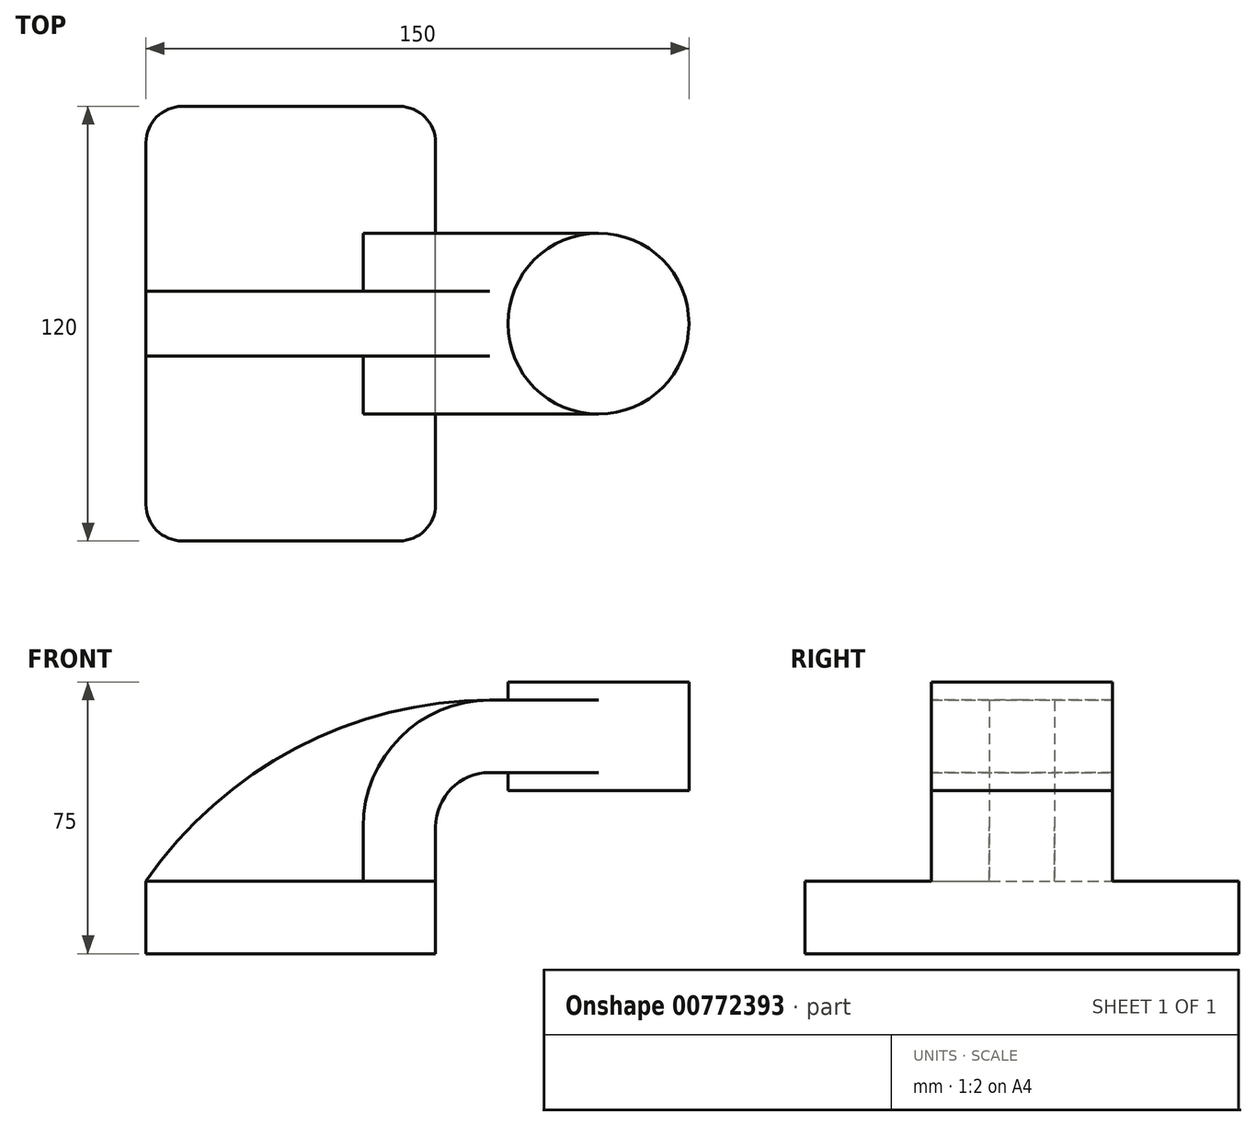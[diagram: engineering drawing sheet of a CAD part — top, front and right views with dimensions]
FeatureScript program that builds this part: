
annotation { "Feature Type Name" : "Feature", "Feature Type Description" : "" }
export const myFeature = defineFeature(function(context is Context, id is Id, definition is map)
    precondition{}
    {
        {
            var Q0;
            Q0=qCreatedBy(makeId("Front.planeOp"),FACE);
            var sketch = newSketch(context, id + "F0", { "sketchPlane" : qUnion([Q0])});
            skLineSegment(sketch, "E0.bottom", {"start": v(0, 0) * mm, "end": v(80, 0) * mm});
            skLineSegment(sketch, "E0.top", {"start": v(0, 20) * mm, "end": v(80, 20) * mm});
            skLineSegment(sketch, "E0.left", {"start": v(0, 0) * mm, "end": v(0, 20) * mm});
            skLineSegment(sketch, "E0.right", {"start": v(80, 0) * mm, "end": v(80, 20) * mm});
            skLineSegment(sketch, "E1", {"start": v(80, 20) * mm, "end": v(80, 35) * mm});
            skLineSegment(sketch, "E2", {"start": v(95, 50) * mm, "end": v(125, 50) * mm});
            skPoint(sketch, "E3.visualSharp", {"position": v(80, 50) * mm});
            skArc(sketch, "E3.filletArc", {"start": v(95, 50) * mm, "mid": v(84.4, 45.6) * mm, "end": v(80, 35) * mm});
            skLineSegment(sketch, "E4.bottom", {"start": v(125, 45) * mm, "end": v(150, 45) * mm});
            skLineSegment(sketch, "E4.top", {"start": v(125, 75) * mm, "end": v(150, 75) * mm});
            skLineSegment(sketch, "E4.left", {"start": v(125, 45) * mm, "end": v(125, 75) * mm});
            skLineSegment(sketch, "E4.right", {"start": v(150, 45) * mm, "end": v(150, 75) * mm});
            skLineSegment(sketch, "E5.0", {"start": v(95, 70) * mm, "end": v(125, 70) * mm});
            skArc(sketch, "E5.1", {"start": v(95, 70) * mm, "mid": v(70.25, 59.75) * mm, "end": v(60, 35) * mm});
            skLineSegment(sketch, "E5.2", {"start": v(60, 20) * mm, "end": v(60, 35) * mm});
            skArc(sketch, "E6", {"start": v(95, 70) * mm, "mid": v(41.32, 56.74) * mm, "end": v(0, 20) * mm});
            skSolve(sketch);
        }
        {
            var Q0;
            Q0=makeQuery(id+"F0.imprint","IMPRINT",FACE,{"disambiguationData":[TD([[makeQuery(id+"F0.imprint","IMPRINT",EDGE,{"derivedFrom":sQuery(id+"F0.wireOp",EDGE,"E0.bottom")}),1.0]])]});
            extrude(context, id + "F1", {"entities" : qUnion([Q0]), "endBound" : BoundingType.SYMMETRIC, "depth" : 120 * mm, "offsetDistance" : 25 * mm});
        }
        {
            var Q0;
            Q0=makeQuery(id+"F0.imprint","IMPRINT",FACE,{"disambiguationData":[TD([[makeQuery(id+"F0.imprint","IMPRINT",EDGE,{"derivedFrom":sQuery(id+"F0.wireOp",EDGE,"E5.1")}),-1.0]])]});
            extrude(context, id + "F2", {"entities" : qUnion([Q0]), "operationType" : NewBodyOperationType.ADD, "endBound" : BoundingType.SYMMETRIC, "depth" : 18 * mm, "offsetDistance" : 25 * mm});
        }
        {
            var Q0;
            {var subQ1=sQuery(id+"F0.wireOp",EDGE,"E1");Q0=makeQuery(id+"F0.imprint","IMPRINT",FACE,{"disambiguationData":[TD([[makeQuery(id+"F0.imprint","IMPRINT",EDGE,{"derivedFrom":subQ1}),1.0]])]});}
            extrude(context, id + "F3", {"entities" : qUnion([Q0]), "operationType" : NewBodyOperationType.ADD, "endBound" : BoundingType.SYMMETRIC, "depth" : 50 * mm, "offsetDistance" : 25 * mm});
        }
        {
            var Q0;
            {var subQ3=sQuery(id+"F0.wireOp",EDGE,"E4.bottom");Q0=makeQuery(id+"F0.imprint","IMPRINT",FACE,{"disambiguationData":[TD([[makeQuery(id+"F0.imprint","IMPRINT",EDGE,{"derivedFrom":subQ3}),1.0]])]});}
            var Q1;
            Q1=sQuery(id+"F0.wireOp",EDGE,"E4.left");
            revolve(context, id + "F4", {"operationType" : NewBodyOperationType.ADD, "surfaceOperationType" : NewSurfaceOperationType.NEW, "entities" : qUnion([Q0]), "axis" : qUnion([Q1]), "revolveType" : RevolveType.FULL});
        }
        {
            var Q0;
            Q0=makeQuery(id+"F1.opExtrude","CAP_EDGE",EDGE,{"disambiguationData":[OSD([sQuery(id+"F0.wireOp",EDGE,"E0.left")])],"isStart":false});
            var Q1;
            Q1=makeQuery(id+"F1.opExtrude","CAP_EDGE",EDGE,{"disambiguationData":[OSD([sQuery(id+"F0.wireOp",EDGE,"E0.right")])],"isStart":false});
            var Q2;
            Q2=makeQuery(id+"F1.opExtrude","CAP_EDGE",EDGE,{"disambiguationData":[OSD([sQuery(id+"F0.wireOp",EDGE,"E0.left")])],"isStart":true});
            var Q3;
            Q3=makeQuery(id+"F1.opExtrude","CAP_EDGE",EDGE,{"disambiguationData":[OSD([sQuery(id+"F0.wireOp",EDGE,"E0.right")])],"isStart":true});
            fillet(context, id + "F5", {"entities" : qUnion([Q0, Q1, Q2, Q3]), "radius" : 10 * mm, "tangentPropagation" : true, "allowEdgeOverflow" : false});
        }
    });
